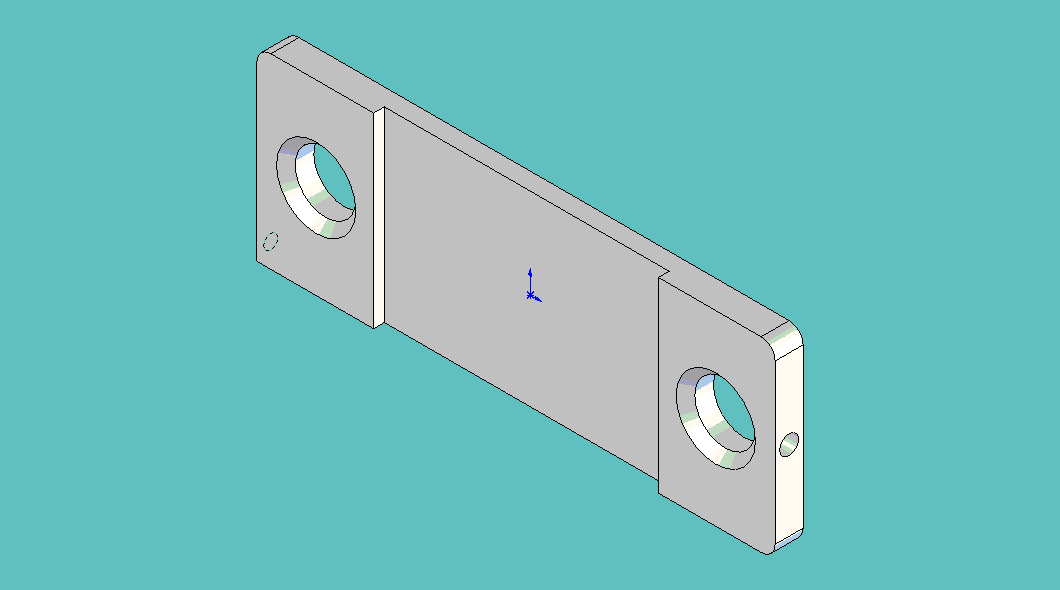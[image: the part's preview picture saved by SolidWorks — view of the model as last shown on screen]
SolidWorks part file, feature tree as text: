
SOLIDWORKS PART (.sldprt)
format: sldprt  version: not decoded by parser v0  size: 327,680 bytes
history: native  units: mm
features: sketch x5, plane x3, hole x2, mirror x2, material x1, extrude x1, fillet x1, chamfer x1, cut_extrude x1, thread x1 (+10 scaffold rows collapsed)
feature tree (28):
  scaffold x10  (default folders/planes/origin — collapsed)
  material  "Matériau <non spécifié>"
  plane  "Plan de face"
  plane  "Plan de dessus"
  plane  "Plan de droite"
  sketch  "Esquisse1"  dims[D5=13.0mm D1=111.0mm D2=40.0mm D3=20.0mm D4=55.5mm D6=85.6mm]
  extrude  "Extrusion1"  Depth=6mm
  fillet  "Congé1"  Radius=3mm
  chamfer  "Chanfrein1"  Distance=2mm Angle=45deg
  sketch  "Esquisse2"  dims[D1=61.0mm D2=30.5mm]
  cut_extrude  "Enlèv. mat.-Extru.1"  Depth=2.3mm
  hole  "Dégagement M1.61"  Diameter=4mm Depth=3.7mm
  sketch  "Esquisse3D1"  dims[c1.D1=~28.23393mm c1.D2=~2.843385mm c1.D3=3.0mm c2.D1=3.0mm c2.D2=20.0mm]
  sketch  "Esquisse3"  dims[hole-wizard template sketch: 46 standard entries collapsed; hole parameters kept: c15.Diamètre du perçage=4.0mm c15.Profondeur du perçage=3.7mm c15.D3=~14.816244mm c15.Angle de pointe=90.0deg]
  mirror  "Symétrie1"
  hole  "Trou taraudé M3x0.51"  [1 undecoded]
  mirror  "Esquisse3D2"
  sketch  "Esquisse4"  dims[hole-wizard template sketch: 47 standard entries collapsed; hole parameters kept: c15.Profondeur du trou pour taraudage=7.5mm c15.D3=~14.816244mm c15.Angle de pointe=118.0deg]
  thread  "Filetage de perçage2"  Diameter=6mm  [1 undecoded]
decode coverage: 11 of 14 modeling features carry decoded parameters
note: ~ marks probable driven/reference dimensions
note: 2 parameter values undecoded
note: suppression state not decoded; provenance and decode notes live in map.json
